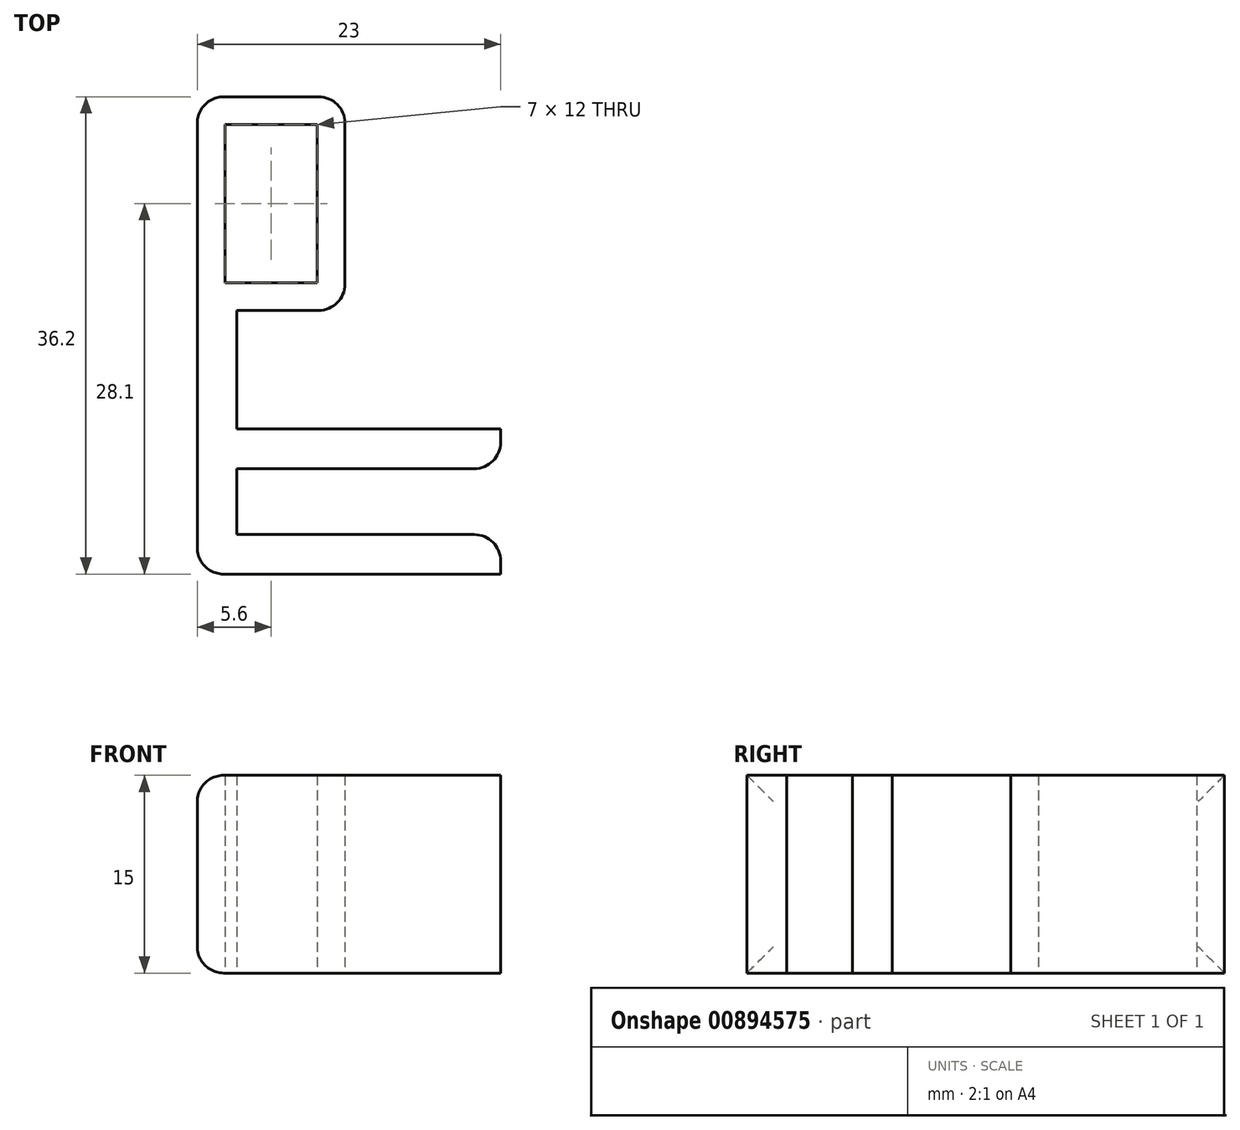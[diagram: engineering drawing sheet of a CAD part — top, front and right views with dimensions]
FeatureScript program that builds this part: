
annotation { "Feature Type Name" : "Feature", "Feature Type Description" : "" }
export const myFeature = defineFeature(function(context is Context, id is Id, definition is map)
    precondition{}
    {
        {
            var Q0;
            Q0=qCreatedBy(makeId("Top.planeOp"),FACE);
            var sketch = newSketch(context, id + "F0", { "sketchPlane" : qUnion([Q0])});
            skLineSegment(sketch, "E0.bottom", {"start": v(-3.5, 6) * mm, "end": v(3.5, 6) * mm});
            skLineSegment(sketch, "E0.top", {"start": v(-3.5, -6) * mm, "end": v(3.5, -6) * mm});
            skLineSegment(sketch, "E0.left", {"start": v(-3.5, 6) * mm, "end": v(-3.5, -6) * mm});
            skLineSegment(sketch, "E0.right", {"start": v(3.5, 6) * mm, "end": v(3.5, -6) * mm});
            skPoint(sketch, "E0.middle", {"position": v(0, 0) * mm});
            skLineSegment(sketch, "E1.0", {"start": v(-5.6, 8.1) * mm, "end": v(5.6, 8.1) * mm});
            skLineSegment(sketch, "E1.1", {"start": v(-5.6, 8.1) * mm, "end": v(-5.6, -8.1) * mm});
            skLineSegment(sketch, "E1.2", {"start": v(-5.6, -8.1) * mm, "end": v(5.6, -8.1) * mm});
            skLineSegment(sketch, "E1.3", {"start": v(5.6, 8.1) * mm, "end": v(5.6, -8.1) * mm});
            skLineSegment(sketch, "E2", {"start": v(-5.6, -8.1) * mm, "end": v(-5.6, -28.1) * mm});
            skLineSegment(sketch, "E3", {"start": v(-5.6, -28.1) * mm, "end": v(17.4, -28.1) * mm});
            skLineSegment(sketch, "E4", {"start": v(17.4, -28.1) * mm, "end": v(17.4, -25.1) * mm});
            skLineSegment(sketch, "E5", {"start": v(17.4, -25.1) * mm, "end": v(-2.6, -25.1) * mm});
            skLineSegment(sketch, "E6", {"start": v(-2.6, -25.1) * mm, "end": v(-2.6, -20.1) * mm});
            skLineSegment(sketch, "E7", {"start": v(-2.6, -20.1) * mm, "end": v(17.4, -20.1) * mm});
            skLineSegment(sketch, "E8", {"start": v(17.4, -20.1) * mm, "end": v(17.4, -17.1) * mm});
            skLineSegment(sketch, "E9", {"start": v(17.4, -17.1) * mm, "end": v(-2.6, -17.1) * mm});
            skLineSegment(sketch, "E10", {"start": v(-2.6, -17.1) * mm, "end": v(-2.6, -8.1) * mm});
            skSolve(sketch);
        }
        {
            var Q0;
            Q0 = qSketchRegion(id + "F0", true);
            extrude(context, id + "F1", {"entities" : qUnion([Q0]), "depth" : 15 * mm, "offsetDistance" : 25 * mm});
        }
        {
            var Q0;
            Q0=makeQuery(id+"F1.opExtrude","SWEPT_FACE",FACE,{"disambiguationData":[OSD([sQuery(id+"F0.wireOp",EDGE,"E1.1"),sQuery(id+"F0.wireOp",EDGE,"E2")])]});
            var Q1;
            Q1=makeQuery(id+"F1.opExtrude","SWEPT_EDGE",EDGE,{"disambiguationData":[OSD([sQuery(id+"F0.wireOp",EDGE,"E7"),sQuery(id+"F0.wireOp",EDGE,"E8")])]});
            var Q2;
            Q2=makeQuery(id+"F1.opExtrude","SWEPT_EDGE",EDGE,{"disambiguationData":[OSD([sQuery(id+"F0.wireOp",EDGE,"E4"),sQuery(id+"F0.wireOp",EDGE,"E5")])]});
            var Q3;
            Q3=makeQuery(id+"F1.opExtrude","SWEPT_EDGE",EDGE,{"disambiguationData":[OSD([sQuery(id+"F0.wireOp",EDGE,"E1.0"),sQuery(id+"F0.wireOp",EDGE,"E1.3")])]});
            var Q4;
            Q4=makeQuery(id+"F1.opExtrude","SWEPT_EDGE",EDGE,{"disambiguationData":[OSD([sQuery(id+"F0.wireOp",EDGE,"E1.2"),sQuery(id+"F0.wireOp",EDGE,"E1.3")])]});
            fillet(context, id + "F2", {"entities" : qUnion([Q0, Q1, Q2, Q3, Q4]), "radius" : 2 * mm, "tangentPropagation" : true, "allowEdgeOverflow" : false});
        }
    });
